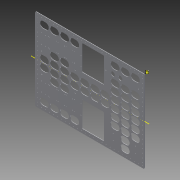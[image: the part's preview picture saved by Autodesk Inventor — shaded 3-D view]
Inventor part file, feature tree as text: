
AUTODESK INVENTOR PART (.ipt)
format: ipt  version: 2014 SP1 (Build 180222100, 222)  size: 895,488 bytes
history: native  units: in
note: dims shown in document units (in); Inventor stores cm internally (conversion verified against a paired STEP export)
features: reference x83, other x11, sketch x10, sheet_metal_op x5, pattern_linear x2, chamfer x1, plane x1, mirror x1, projected_geometry x1
ambient origin geometry x8: Origin, YZ Plane, XZ Plane, XY Plane, X Axis, Y Axis, Z Axis, Center Point
bodies: Solid1 (feature_tree)
feature tree (115):
  sheet_metal_op  "Face1"
  pattern_linear  "Rectangular Pattern2"  Count1=27 Spacing1=1.0in
  pattern_linear  "Rectangular Pattern5"  Spacing1=0.125in  [1 undecoded]
  sheet_metal_op  "Face4"
  sheet_metal_op  "Face5"
  sketch  "Sketch22"  dims[d18=0.0in d19=10.6299in d21=1.0in]
  chamfer  "Corner Round1"
  plane  "Work Plane1"
  mirror  "Mirror1"
  sketch  "Sketch1"  dims[d0=27.0in]
  other  "Plate1"
  sketch  "Sketch2"  dims[d1=20.325in]
  sketch  "Sketch4"  dims[d2=0.125in]
  reference  "Reference4"
  reference  "Reference5"
  sketch  "Sketch12"  dims[d4=7.25in]
  reference  "Reference10"
  reference  "Reference11"
  sketch  "Sketch16"  dims[d5=5.5in]
  reference  "Reference12"
  reference  "Reference13"
  reference  "Reference14"
  reference  "Reference15"
  reference  "Reference16"
  reference  "Reference17"
  reference  "Reference18"
  reference  "Reference19"
  reference  "Reference20"
  reference  "Reference21"
  reference  "Reference22"
  reference  "Reference23"
  reference  "Reference24"
  reference  "Reference25"
  reference  "Reference26"
  reference  "Reference27"
  reference  "Reference28"
  reference  "Reference29"
  reference  "Reference30"
  reference  "Reference31"
  reference  "Reference32"
  reference  "Reference33"
  reference  "Reference34"
  reference  "Reference35"
  reference  "Reference36"
  reference  "Reference37"
  reference  "Reference38"
  reference  "Reference39"
  reference  "Reference40"
  reference  "Reference41"
  reference  "Reference42"
  reference  "Reference43"
  reference  "Reference44"
  reference  "Reference45"
  reference  "Reference46"
  projected_geometry  "Projected Loop1"
  reference  "Reference47"
  reference  "Reference48"
  reference  "Reference49"
  reference  "Reference50"
  reference  "Reference51"
  reference  "Reference52"
  reference  "Reference53"
  reference  "Reference54"
  reference  "Reference55"
  reference  "Reference56"
  reference  "Reference57"
  reference  "Reference58"
  reference  "Reference59"
  reference  "Reference60"
  reference  "Reference61"
  reference  "Reference62"
  reference  "Reference63"
  reference  "Reference64"
  reference  "Reference65"
  reference  "Reference66"
  reference  "Reference67"
  reference  "Reference68"
  reference  "Reference69"
  reference  "Reference70"
  reference  "Reference71"
  reference  "Reference72"
  reference  "Reference73"
  reference  "Reference74"
  reference  "Reference75"
  reference  "Reference76"
  reference  "Reference77"
  reference  "Reference78"
  reference  "Reference79"
  reference  "Reference80"
  reference  "Reference81"
  reference  "Reference82"
  reference  "Reference83"
  reference  "Reference84"
  reference  "Reference85"
  reference  "Reference86"
  reference  "Reference87"
  reference  "Reference88"
  sketch  "Sketch19"  dims[d6=7.25in]
  other  "Plate4"
  sheet_metal_op  "Bend3"
  sketch  "Sketch21"  dims[d17=0.125in]
  other  "Plate5"
  sheet_metal_op  "Bend4"
  sketch  "Sketch24"  dims[d23=1.0in]
  reference  "Reference89"
  reference  "Reference90"
  sketch  "Sketch25"  dims[d24=1.0in d65=0.125in d66=0.0in d78=11.55in d79=5.5in d80=11.55in d97=0.125in d98=0.0in d99=7.4803in d101=1.0in d102=0.7874in d104=26.0in d105=0.125in d106=0.0in d107=1.0in d109=1.8325in d110=2.5in d111=0.125in d112=3.937in d114=1.8325in d115=3.937in d117=2.5in d122=0.125in d123=0.125in d124=0.0625in d125=0.25in d126=0.125in d127=0.125in d128=0.125in d129=0.0625in d130=0.25in d131=0.125in d132=0.25in d133=2.8579in d134=1.57in d135=2.29in d136=0.171in d137=0.171in d138=0.125in d139=0.0in d140=-10.1625in d141=1.75in d142=0.266in d143=4.5in d144=0.266in d145=0.125in d146=0.0in d147=1.0in d148=1.0in d149=0.125in d150=0.0in d151=0.125in d152=0.0in]
  other  "Cut3"
  other  "Cut6"
  other  "Cut8"
  other  "Cut9"
  other  "Cut11"
  other  "Cut12"
  other  "Cut13"
  other  "Cut14"
note: 1 required parameter value undecoded (feature->parameter linkage not recoverable at this tier; creation-order binding heuristic only, values carry confidence <= 0.55)
